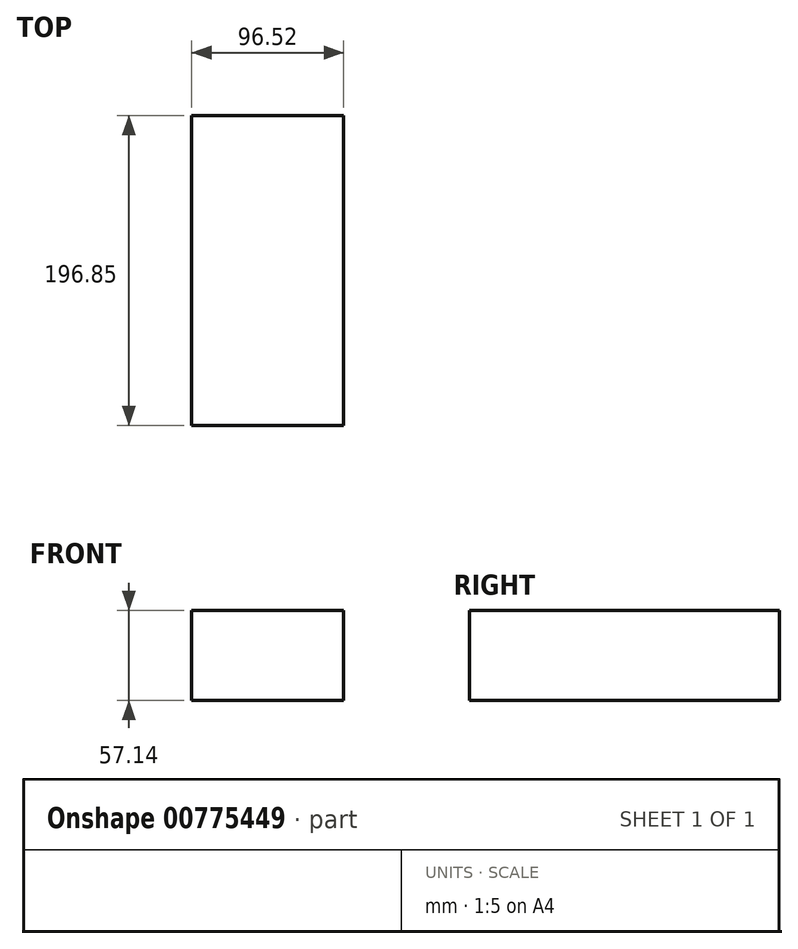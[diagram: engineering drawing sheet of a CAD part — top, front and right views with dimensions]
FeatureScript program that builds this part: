
annotation { "Feature Type Name" : "Feature", "Feature Type Description" : "" }
export const myFeature = defineFeature(function(context is Context, id is Id, definition is map)
    precondition{}
    {
        {
            var Q0;
            Q0=qCreatedBy(makeId("Front.planeOp"),FACE);
            var sketch = newSketch(context, id + "F0", { "sketchPlane" : qUnion([Q0])});
            skLineSegment(sketch, "E0.bottom", {"start": v(-48.26, 28.58) * mm, "end": v(48.26, 28.58) * mm});
            skLineSegment(sketch, "E0.top", {"start": v(-48.26, -28.57) * mm, "end": v(48.26, -28.57) * mm});
            skLineSegment(sketch, "E0.left", {"start": v(-48.26, 28.58) * mm, "end": v(-48.26, -28.57) * mm});
            skLineSegment(sketch, "E0.right", {"start": v(48.26, 28.58) * mm, "end": v(48.26, -28.57) * mm});
            skPoint(sketch, "E0.middle", {"position": v(0, 0) * mm});
            skSolve(sketch);
        }
        {
            var Q0;
            Q0 = qSketchRegion(id + "F0", true);
            extrude(context, id + "F1", {"entities" : qUnion([Q0]), "flatOperationType" : FlatOperationType.REMOVE, "depth" : 196.85 * mm, "offsetDistance" : 25.4 * mm, "domain" : OperationDomain.MODEL});
        }
    });
